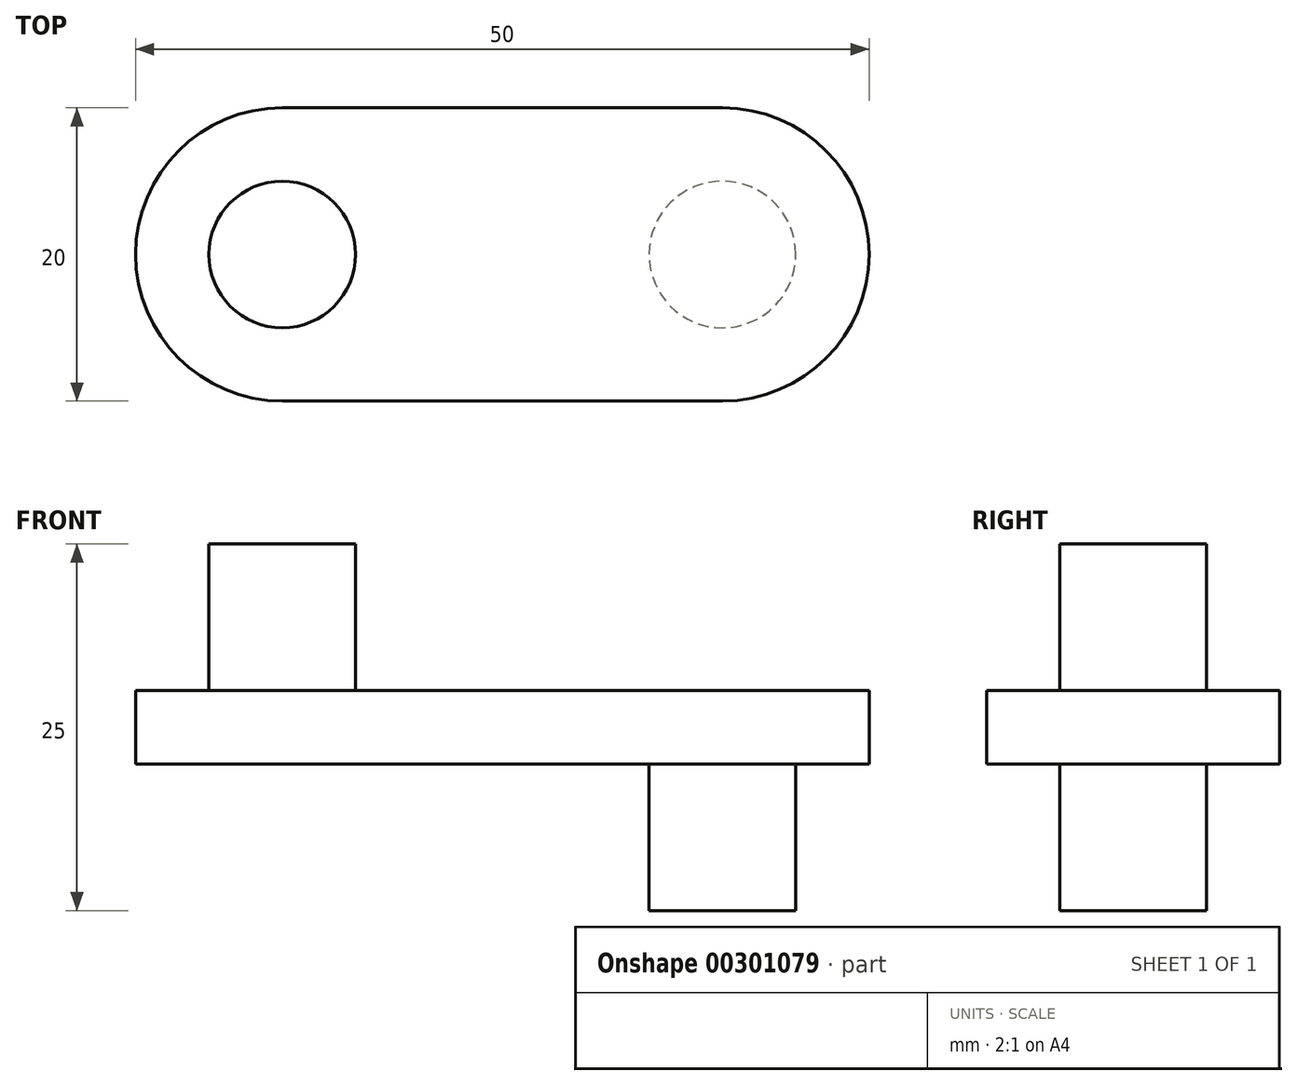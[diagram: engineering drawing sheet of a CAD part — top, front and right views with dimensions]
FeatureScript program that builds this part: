
annotation { "Feature Type Name" : "Feature", "Feature Type Description" : "" }
export const myFeature = defineFeature(function(context is Context, id is Id, definition is map)
    precondition{}
    {
        {
            var Q0;
            Q0=qCreatedBy(makeId("Top.planeOp"),FACE);
            var sketch = newSketch(context, id + "F0", { "sketchPlane" : qUnion([Q0])});
            skLineSegment(sketch, "E0", {"start": v(0, 20) * mm, "end": v(30, 20) * mm});
            skLineSegment(sketch, "E1", {"start": v(0, 0) * mm, "end": v(30, 0) * mm});
            skArc(sketch, "E2", {"start": v(30, 0) * mm, "mid": v(40, 10) * mm, "end": v(30, 20) * mm});
            skArc(sketch, "E3", {"start": v(0, 20) * mm, "mid": v(-10, 10) * mm, "end": v(0, 0) * mm});
            skCircle(sketch, "E4", {"center": v(0, 10) * mm, "radius": 5 * mm});
            skCircle(sketch, "E5", {"center": v(30, 10) * mm, "radius": 5 * mm});
            skSolve(sketch);
        }
        {
            var Q0;
            Q0=makeQuery(id+"F0.imprint","IMPRINT",FACE,{"disambiguationData":[TD([[makeQuery(id+"F0.imprint","IMPRINT",EDGE,{"derivedFrom":sQuery(id+"F0.wireOp",EDGE,"E0")}),-1.0]])]});
            extrude(context, id + "F1", {"entities" : qUnion([Q0]), "depth" : 5 * mm});
        }
        {
            var Q0;
            Q0=makeQuery(id+"F0.imprint","IMPRINT",FACE,{"disambiguationData":[TD([[makeQuery(id+"F0.imprint","IMPRINT",EDGE,{"derivedFrom":sQuery(id+"F0.wireOp",EDGE,"E4")}),1.0]])]});
            extrude(context, id + "F2", {"entities" : qUnion([Q0]), "operationType" : NewBodyOperationType.ADD, "depth" : 15 * mm});
        }
        {
            var Q0;
            Q0=makeQuery(id+"F0.imprint","IMPRINT",FACE,{"disambiguationData":[TD([[makeQuery(id+"F0.imprint","IMPRINT",EDGE,{"derivedFrom":sQuery(id+"F0.wireOp",EDGE,"E5")}),1.0]])]});
            extrude(context, id + "F3", {"entities" : qUnion([Q0]), "operationType" : NewBodyOperationType.ADD, "depth" : 5 * mm, "hasSecondDirection" : true, "secondDirectionOppositeDirection" : true, "secondDirectionDepth" : 10 * mm});
        }
    });
